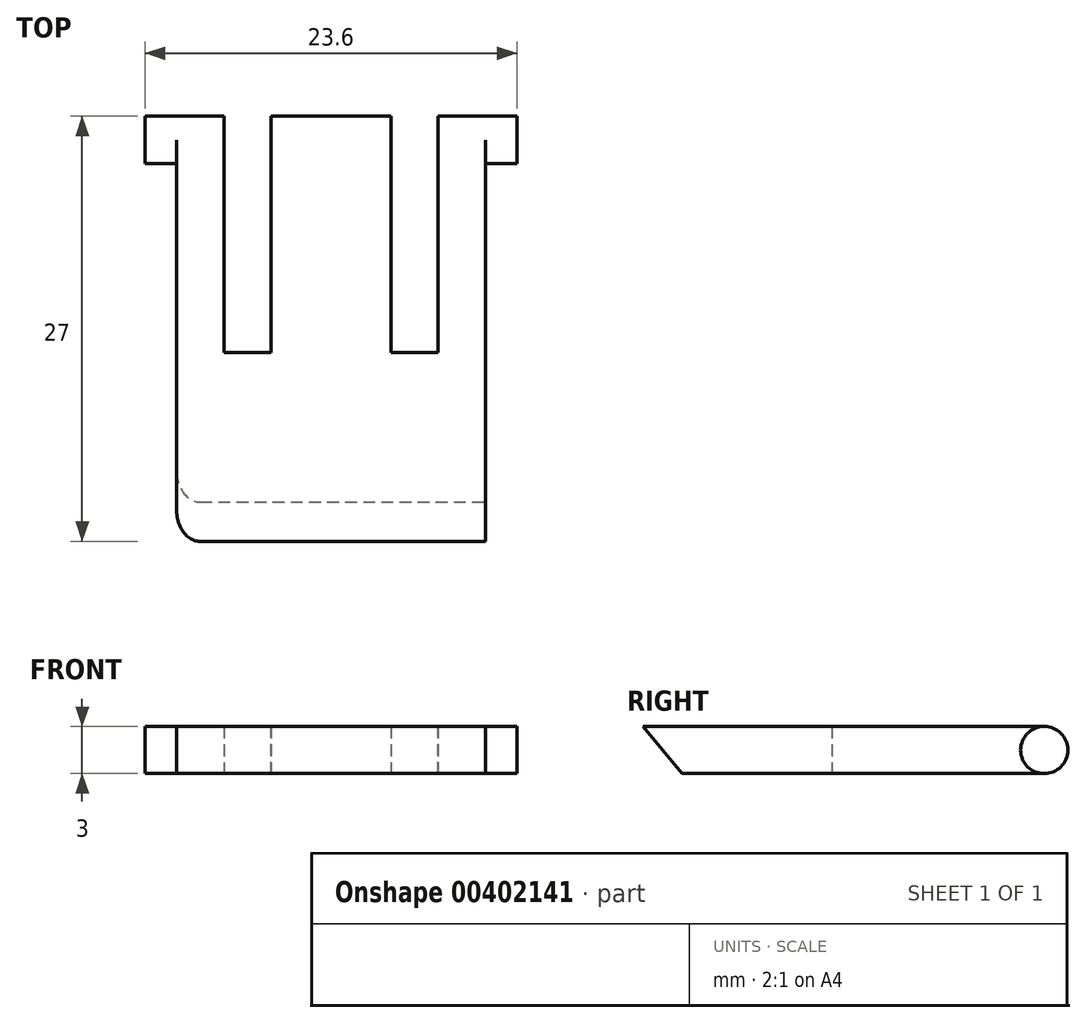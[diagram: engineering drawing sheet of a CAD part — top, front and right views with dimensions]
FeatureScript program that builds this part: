
annotation { "Feature Type Name" : "Feature", "Feature Type Description" : "" }
export const myFeature = defineFeature(function(context is Context, id is Id, definition is map)
    precondition{}
    {
        {
            var Q0;
            Q0=qCreatedBy(makeId("Top.planeOp"),FACE);
            var sketch = newSketch(context, id + "F0", { "sketchPlane" : qUnion([Q0])});
            skLineSegment(sketch, "E0", {"start": v(-9.8, 0) * mm, "end": v(9.8, 0) * mm});
            skLineSegment(sketch, "E1", {"start": v(9.8, 0) * mm, "end": v(9.8, 27) * mm});
            skLineSegment(sketch, "E2", {"start": v(9.8, 27) * mm, "end": v(6.8, 27) * mm});
            skLineSegment(sketch, "E3", {"start": v(6.8, 27) * mm, "end": v(6.8, 12) * mm});
            skLineSegment(sketch, "E4", {"start": v(6.8, 12) * mm, "end": v(3.8, 12) * mm});
            skLineSegment(sketch, "E5", {"start": v(3.8, 12) * mm, "end": v(3.8, 27) * mm});
            skLineSegment(sketch, "E6", {"start": v(3.8, 27) * mm, "end": v(-3.8, 27) * mm});
            skLineSegment(sketch, "E7", {"start": v(-3.8, 27) * mm, "end": v(-3.8, 12) * mm});
            skLineSegment(sketch, "E8", {"start": v(-3.8, 12) * mm, "end": v(-6.8, 12) * mm});
            skLineSegment(sketch, "E9", {"start": v(-6.8, 12) * mm, "end": v(-6.8, 27) * mm});
            skLineSegment(sketch, "E10", {"start": v(-6.8, 27) * mm, "end": v(-9.8, 27) * mm});
            skLineSegment(sketch, "E11", {"start": v(-9.8, 27) * mm, "end": v(-9.8, 0) * mm});
            skLineSegment(sketch, "E12", {"start": v(-9.8, 0) * mm, "end": v(-9.8, 0) * mm});
            skSolve(sketch);
        }
        {
            var Q0;
            Q0=makeQuery(id+"F0.imprint","IMPRINT",FACE,{"disambiguationData":[TD([[makeQuery(id+"F0.imprint","IMPRINT",EDGE,{"derivedFrom":sQuery(id+"F0.wireOp",EDGE,"E0")}),1.0]])]});
            extrude(context, id + "F1", {"entities" : qUnion([Q0]), "depth" : 3 * mm});
        }
        {
            var Q0;
            Q0=makeQuery(id+"F1.opExtrude","SWEPT_FACE",FACE,{"disambiguationData":[OSD([sQuery(id+"F0.wireOp",EDGE,"E1")])]});
            var sketch = newSketch(context, id + "F2", { "sketchPlane" : qUnion([Q0])});
            skLineSegment(sketch, "E13", {"start": v(0, 1.5) * mm, "end": v(27, 1.5) * mm, "construction": true});
            skLineSegment(sketch, "E14", {"start": v(25.5, 4.65) * mm, "end": v(25.5, -2.43) * mm, "construction": true});
            skCircle(sketch, "E15", {"center": v(25.5, 1.5) * mm, "radius": 1.5 * mm});
            skSolve(sketch);
        }
        {
            var Q0;
            Q0 = qSketchRegion(id + "F2", true);
            extrude(context, id + "F3", {"entities" : qUnion([Q0]), "operationType" : NewBodyOperationType.ADD, "depth" : 2 * mm});
        }
        {
            var Q0;
            {var subQ0=sQuery(id+"F0.wireOp",EDGE,"E1");var subQ1=makeQuery(id+"F1.opExtrude","SWEPT_FACE",FACE,{"disambiguationData":[OSD([subQ0])]});var subQ2=sQuery(id+"F0.wireOp",EDGE,"E11");var subQ3=sQuery(id+"F0.wireOp",EDGE,"E10");var subQ4=sQuery(id+"F0.wireOp",EDGE,"E9");var subQ5=sQuery(id+"F0.wireOp",EDGE,"E8");var subQ6=sQuery(id+"F0.wireOp",EDGE,"E7");var subQ7=sQuery(id+"F0.wireOp",EDGE,"E6");var subQ8=sQuery(id+"F0.wireOp",EDGE,"E5");var subQ9=sQuery(id+"F0.wireOp",EDGE,"E4");var subQ10=sQuery(id+"F0.wireOp",EDGE,"E3");var subQ11=sQuery(id+"F0.wireOp",EDGE,"E2");var subQ12=sQuery(id+"F0.wireOp",EDGE,"E0");Q0=makeQuery(id+"F3.boolean.opBoolean","SPLIT",FACE,{"disambiguationData":[TD([makeQuery(id+"F1.opExtrude","SWEPT_FACE",FACE,{"disambiguationData":[OSD([subQ12])]}),makeQuery(id+"F1.opExtrude","CAP_FACE",FACE,{"disambiguationData":[OSD([subQ12,subQ0,subQ11,subQ10,subQ9,subQ8,subQ7,subQ6,subQ5,subQ4,subQ3,subQ2])],"isStart":true}),makeQuery(id+"F1.opExtrude","CAP_FACE",FACE,{"disambiguationData":[OSD([subQ12,subQ0,subQ11,subQ10,subQ9,subQ8,subQ7,subQ6,subQ5,subQ4,subQ3,subQ2])],"isStart":false}),subQ1,makeQuery(id+"F3.opExtrude","SWEPT_FACE",FACE,{"disambiguationData":[OSD([sQuery(id+"F2.wireOp",EDGE,"E15")])]})])],"derivedFrom":subQ1});}
            var Q1;
            Q1=makeQuery(id+"F1.opExtrude","SWEPT_FACE",FACE,{"disambiguationData":[OSD([sQuery(id+"F0.wireOp",EDGE,"E11")])]});
            cPlane(context, id + "F4", {"entities" : qUnion([Q0, Q1]), "cplaneType" : CPlaneType.MID_PLANE, "offset" : 25 * mm, "width" : 150 * mm, "height" : 150 * mm});
        }
        {
            var Q0;
            Q0=makeQuery(id+"F1.opExtrude","SWEPT_BODY",BODY,{"disambiguationData":[OSD([sQuery(id+"F0.wireOp",EDGE,"E0"),sQuery(id+"F0.wireOp",EDGE,"E1"),sQuery(id+"F0.wireOp",EDGE,"E2"),sQuery(id+"F0.wireOp",EDGE,"E3"),sQuery(id+"F0.wireOp",EDGE,"E4"),sQuery(id+"F0.wireOp",EDGE,"E5"),sQuery(id+"F0.wireOp",EDGE,"E6"),sQuery(id+"F0.wireOp",EDGE,"E7"),sQuery(id+"F0.wireOp",EDGE,"E8"),sQuery(id+"F0.wireOp",EDGE,"E9"),sQuery(id+"F0.wireOp",EDGE,"E10"),sQuery(id+"F0.wireOp",EDGE,"E11")])]});
            var Q1;
            Q1=qCreatedBy(id+"F4.planeOp",FACE);
            mirror(context, id + "F5", {"operationType" : NewBodyOperationType.ADD, "entities" : qUnion([Q0]), "mirrorPlane" : qUnion([Q1])});
        }
        {
            var Q0;
            {var subQ0=sQuery(id+"F0.wireOp",EDGE,"E11");var subQ1=sQuery(id+"F0.wireOp",EDGE,"E10");var subQ2=makeQuery(id+"F1.opExtrude","SWEPT_FACE",FACE,{"disambiguationData":[OSD([subQ0])]});Q0=makeQuery(id+"F5.boolean.opBoolean","SPLIT",FACE,{"disambiguationData":[TD([makeQuery(id+"F1.opExtrude","CAP_FACE",FACE,{"disambiguationData":[OSD([sQuery(id+"F0.wireOp",EDGE,"E0"),sQuery(id+"F0.wireOp",EDGE,"E1"),sQuery(id+"F0.wireOp",EDGE,"E2"),sQuery(id+"F0.wireOp",EDGE,"E3"),sQuery(id+"F0.wireOp",EDGE,"E4"),sQuery(id+"F0.wireOp",EDGE,"E5"),sQuery(id+"F0.wireOp",EDGE,"E6"),sQuery(id+"F0.wireOp",EDGE,"E7"),sQuery(id+"F0.wireOp",EDGE,"E8"),sQuery(id+"F0.wireOp",EDGE,"E9"),subQ1,subQ0])],"isStart":true}),makeQuery(id+"F1.opExtrude","SWEPT_FACE",FACE,{"disambiguationData":[OSD([subQ1])]}),subQ2,makeQuery(id+"F5.opPattern","COPY",FACE,{"derivedFrom":makeQuery(id+"F3.opExtrude","SWEPT_FACE",FACE,{"disambiguationData":[OSD([sQuery(id+"F2.wireOp",EDGE,"E15")])]}),"instanceName":"1"})])],"derivedFrom":subQ2});}
            var Q1;
            {var subQ0=sQuery(id+"F0.wireOp",EDGE,"E11");var subQ1=sQuery(id+"F0.wireOp",EDGE,"E10");var subQ2=makeQuery(id+"F1.opExtrude","SWEPT_FACE",FACE,{"disambiguationData":[OSD([subQ0])]});Q1=makeQuery(id+"F5.boolean.opBoolean","SPLIT",FACE,{"disambiguationData":[TD([makeQuery(id+"F1.opExtrude","CAP_FACE",FACE,{"disambiguationData":[OSD([sQuery(id+"F0.wireOp",EDGE,"E0"),sQuery(id+"F0.wireOp",EDGE,"E1"),sQuery(id+"F0.wireOp",EDGE,"E2"),sQuery(id+"F0.wireOp",EDGE,"E3"),sQuery(id+"F0.wireOp",EDGE,"E4"),sQuery(id+"F0.wireOp",EDGE,"E5"),sQuery(id+"F0.wireOp",EDGE,"E6"),sQuery(id+"F0.wireOp",EDGE,"E7"),sQuery(id+"F0.wireOp",EDGE,"E8"),sQuery(id+"F0.wireOp",EDGE,"E9"),subQ1,subQ0])],"isStart":false}),makeQuery(id+"F1.opExtrude","SWEPT_FACE",FACE,{"disambiguationData":[OSD([subQ1])]}),subQ2,makeQuery(id+"F5.opPattern","COPY",FACE,{"derivedFrom":makeQuery(id+"F3.opExtrude","SWEPT_FACE",FACE,{"disambiguationData":[OSD([sQuery(id+"F2.wireOp",EDGE,"E15")])]}),"instanceName":"1"})])],"derivedFrom":subQ2});}
            extrude(context, id + "F6", {"entities" : qUnion([Q0, Q1]), "operationType" : NewBodyOperationType.REMOVE, "oppositeDirection" : true, "depth" : 25 * mm});
        }
        {
            var Q0;
            {var subQ0=sQuery(id+"F0.wireOp",EDGE,"E1");var subQ1=makeQuery(id+"F1.opExtrude","SWEPT_FACE",FACE,{"disambiguationData":[OSD([subQ0])]});var subQ2=sQuery(id+"F0.wireOp",EDGE,"E11");var subQ3=sQuery(id+"F0.wireOp",EDGE,"E10");var subQ4=sQuery(id+"F0.wireOp",EDGE,"E9");var subQ5=sQuery(id+"F0.wireOp",EDGE,"E8");var subQ6=sQuery(id+"F0.wireOp",EDGE,"E7");var subQ7=sQuery(id+"F0.wireOp",EDGE,"E6");var subQ8=sQuery(id+"F0.wireOp",EDGE,"E5");var subQ9=sQuery(id+"F0.wireOp",EDGE,"E4");var subQ10=sQuery(id+"F0.wireOp",EDGE,"E3");var subQ11=sQuery(id+"F0.wireOp",EDGE,"E2");var subQ12=sQuery(id+"F0.wireOp",EDGE,"E0");Q0=makeQuery(id+"F3.boolean.opBoolean","SPLIT",FACE,{"disambiguationData":[TD([makeQuery(id+"F1.opExtrude","SWEPT_FACE",FACE,{"disambiguationData":[OSD([subQ12])]}),makeQuery(id+"F1.opExtrude","CAP_FACE",FACE,{"disambiguationData":[OSD([subQ12,subQ0,subQ11,subQ10,subQ9,subQ8,subQ7,subQ6,subQ5,subQ4,subQ3,subQ2])],"isStart":true}),makeQuery(id+"F1.opExtrude","CAP_FACE",FACE,{"disambiguationData":[OSD([subQ12,subQ0,subQ11,subQ10,subQ9,subQ8,subQ7,subQ6,subQ5,subQ4,subQ3,subQ2])],"isStart":false}),subQ1,makeQuery(id+"F3.opExtrude","SWEPT_FACE",FACE,{"disambiguationData":[OSD([sQuery(id+"F2.wireOp",EDGE,"E15")])]})])],"derivedFrom":subQ1});}
            var sketch = newSketch(context, id + "F7", { "sketchPlane" : qUnion([Q0])});
            skLineSegment(sketch, "E16", {"start": v(0, 0) * mm, "end": v(2.5, 0) * mm});
            skLineSegment(sketch, "E17", {"start": v(2.5, 0) * mm, "end": v(0, 3) * mm});
            skLineSegment(sketch, "E18", {"start": v(0, 3) * mm, "end": v(0, 0) * mm});
            skSolve(sketch);
        }
        {
            var Q0;
            Q0=makeQuery(id+"F7.imprint","IMPRINT",FACE,{"disambiguationData":[TD([[makeQuery(id+"F7.imprint","IMPRINT",EDGE,{"derivedFrom":sQuery(id+"F7.wireOp",EDGE,"E16")}),1.0]])]});
            extrude(context, id + "F8", {"entities" : qUnion([Q0]), "operationType" : NewBodyOperationType.REMOVE, "oppositeDirection" : true, "depth" : 25 * mm});
        }
        {
            var Q0;
            {var subQ0=sQuery(id+"F0.wireOp",EDGE,"E11");var subQ1=makeQuery(id+"F1.opExtrude","SWEPT_FACE",FACE,{"disambiguationData":[OSD([subQ0])]});var subQ2=sQuery(id+"F0.wireOp",EDGE,"E10");var subQ3=sQuery(id+"F0.wireOp",EDGE,"E9");var subQ4=sQuery(id+"F0.wireOp",EDGE,"E8");var subQ5=sQuery(id+"F0.wireOp",EDGE,"E7");var subQ6=sQuery(id+"F0.wireOp",EDGE,"E6");var subQ7=sQuery(id+"F0.wireOp",EDGE,"E5");var subQ8=sQuery(id+"F0.wireOp",EDGE,"E4");var subQ9=sQuery(id+"F0.wireOp",EDGE,"E3");var subQ10=sQuery(id+"F0.wireOp",EDGE,"E2");var subQ11=sQuery(id+"F0.wireOp",EDGE,"E1");var subQ12=sQuery(id+"F0.wireOp",EDGE,"E0");Q0=makeQuery(id+"F8.boolean.opBoolean","INTERSECT",EDGE,{"derivedFrom":[makeQuery(id+"F5.boolean.opBoolean","SPLIT",FACE,{"disambiguationData":[TD([makeQuery(id+"F1.opExtrude","SWEPT_FACE",FACE,{"disambiguationData":[OSD([subQ12])]}),makeQuery(id+"F1.opExtrude","CAP_FACE",FACE,{"disambiguationData":[OSD([subQ12,subQ11,subQ10,subQ9,subQ8,subQ7,subQ6,subQ5,subQ4,subQ3,subQ2,subQ0])],"isStart":true}),makeQuery(id+"F1.opExtrude","CAP_FACE",FACE,{"disambiguationData":[OSD([subQ12,subQ11,subQ10,subQ9,subQ8,subQ7,subQ6,subQ5,subQ4,subQ3,subQ2,subQ0])],"isStart":false}),subQ1,makeQuery(id+"F5.opPattern","COPY",FACE,{"derivedFrom":makeQuery(id+"F3.opExtrude","SWEPT_FACE",FACE,{"disambiguationData":[OSD([sQuery(id+"F2.wireOp",EDGE,"E15")])]}),"instanceName":"1"})])],"derivedFrom":subQ1}),makeQuery(id+"F8.opExtrude","SWEPT_FACE",FACE,{"disambiguationData":[OSD([sQuery(id+"F7.wireOp",EDGE,"E17")])]})]});}
            var Q1;
            Q1=makeQuery(id+"F8.boolean.opBoolean","COPY",EDGE,{"derivedFrom":makeQuery(id+"F8.opExtrude","CAP_EDGE",EDGE,{"disambiguationData":[OSD([sQuery(id+"F7.wireOp",EDGE,"E17")])],"isStart":true})});
            fillet(context, id + "F9", {"entities" : qUnion([Q0, Q1]), "radius" : 1.5 * mm, "tangentPropagation" : true, "allowEdgeOverflow" : false});
        }
    });
